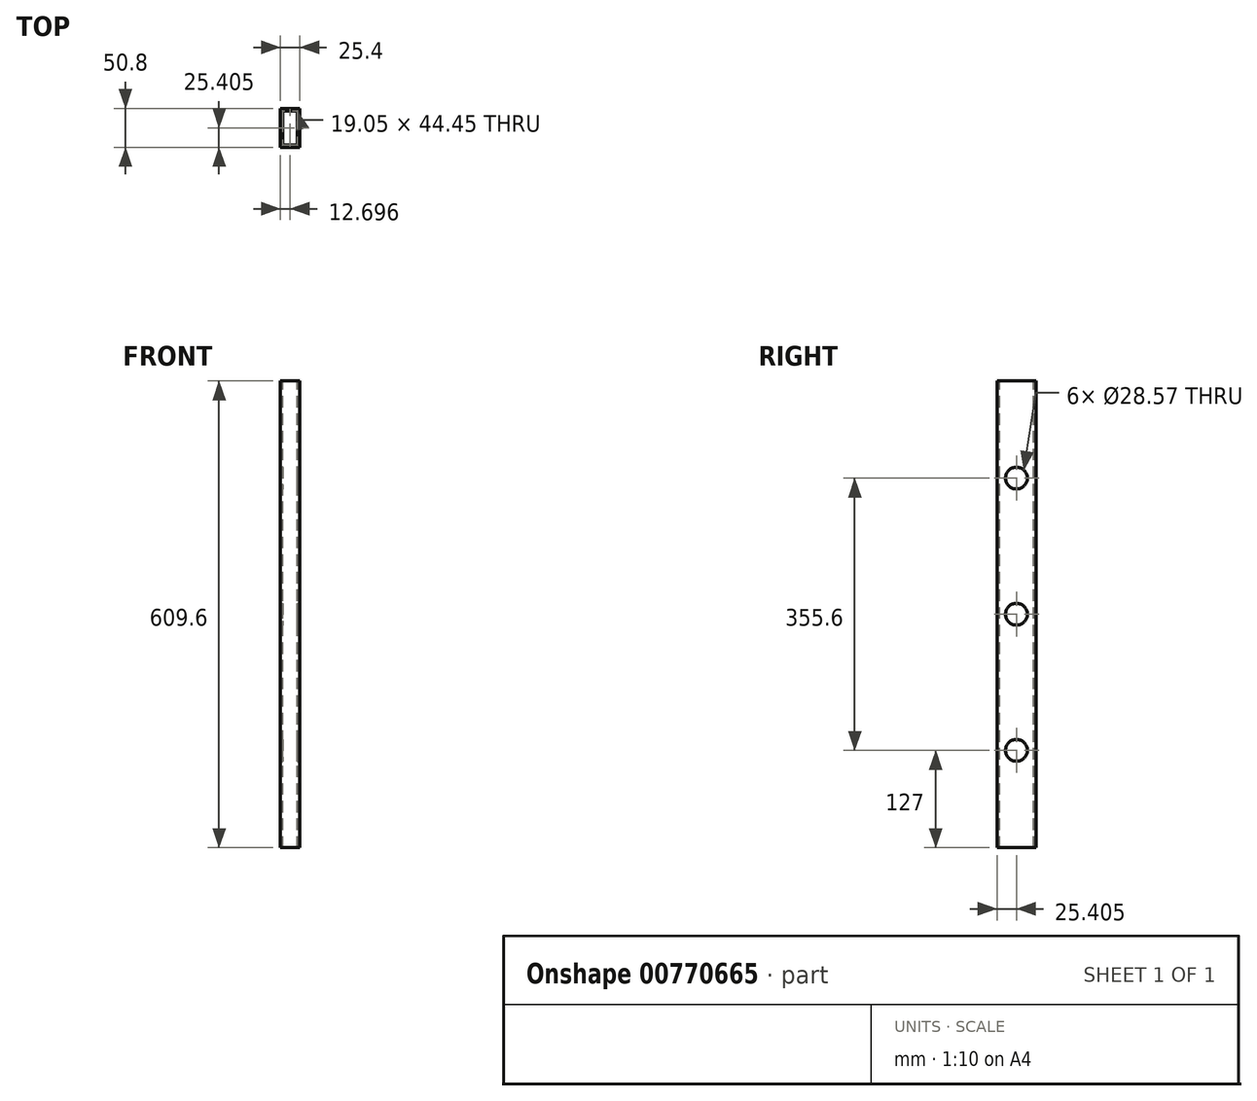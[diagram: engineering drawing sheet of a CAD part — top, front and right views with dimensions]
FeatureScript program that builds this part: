
annotation { "Feature Type Name" : "Feature", "Feature Type Description" : "" }
export const myFeature = defineFeature(function(context is Context, id is Id, definition is map)
    precondition{}
    {
        {
            var Q0;
            Q0=qCreatedBy(makeId("Top.planeOp"),FACE);
            var sketch = newSketch(context, id + "F0", { "sketchPlane" : qUnion([Q0])});
            skLineSegment(sketch, "E0.bottom", {"start": v(-17.82, 49.84) * mm, "end": v(7.58, 49.84) * mm});
            skLineSegment(sketch, "E0.top", {"start": v(-17.82, -0.96) * mm, "end": v(7.58, -0.96) * mm});
            skLineSegment(sketch, "E0.left", {"start": v(-17.82, 49.84) * mm, "end": v(-17.82, -0.96) * mm});
            skLineSegment(sketch, "E0.right", {"start": v(7.58, 49.84) * mm, "end": v(7.58, -0.96) * mm});
            skSolve(sketch);
        }
        {
            var Q0;
            Q0 = qSketchRegion(id + "F0", true);
            extrude(context, id + "F1", {"entities" : qUnion([Q0]), "depth" : 609.6 * mm, "offsetDistance" : 25.4 * mm});
        }
        {
            var Q0;
            Q0=makeQuery(id+"F1.opExtrude","CAP_FACE",FACE,{"disambiguationData":[OSD([sQuery(id+"F0.wireOp",EDGE,"E0.bottom"),sQuery(id+"F0.wireOp",EDGE,"E0.top"),sQuery(id+"F0.wireOp",EDGE,"E0.left"),sQuery(id+"F0.wireOp",EDGE,"E0.right")])],"isStart":false});
            var sketch = newSketch(context, id + "F2", { "sketchPlane" : qUnion([Q0])});
            skLineSegment(sketch, "E1.bottom", {"start": v(-14.65, 46.67) * mm, "end": v(4.4, 46.67) * mm});
            skLineSegment(sketch, "E1.top", {"start": v(-14.65, 2.22) * mm, "end": v(4.4, 2.22) * mm});
            skLineSegment(sketch, "E1.left", {"start": v(-14.65, 46.67) * mm, "end": v(-14.65, 2.22) * mm});
            skLineSegment(sketch, "E1.right", {"start": v(4.4, 46.67) * mm, "end": v(4.4, 2.22) * mm});
            skSolve(sketch);
        }
        {
            var Q0;
            Q0=makeQuery(id+"F2.imprint","IMPRINT",FACE,{"disambiguationData":[TD([[makeQuery(id+"F2.imprint","IMPRINT",EDGE,{"derivedFrom":sQuery(id+"F2.wireOp",EDGE,"E1.bottom")}),-1.0]])]});
            extrude(context, id + "F3", {"entities" : qUnion([Q0]), "operationType" : NewBodyOperationType.REMOVE, "oppositeDirection" : true, "depth" : 670.56 * mm, "offsetDistance" : 25.4 * mm});
        }
        {
            var Q0;
            Q0=makeQuery(id+"F1.opExtrude","SWEPT_FACE",FACE,{"disambiguationData":[OSD([sQuery(id+"F0.wireOp",EDGE,"E0.right")])]});
            var sketch = newSketch(context, id + "F4", { "sketchPlane" : qUnion([Q0])});
            skCircle(sketch, "E2", {"center": v(24.44, 304.8) * mm, "radius": 14.29 * mm});
            skCircle(sketch, "E3", {"center": v(24.44, 482.6) * mm, "radius": 14.29 * mm});
            skPoint(sketch, "E4.centerSnap0", {"position": v(24.44, 0) * mm});
            skCircle(sketch, "E5", {"center": v(24.44, 127) * mm, "radius": 14.29 * mm});
            skSolve(sketch);
        }
        {
            var Q0;
            Q0=makeQuery(id+"F4.imprint","IMPRINT",FACE,{"disambiguationData":[TD([[makeQuery(id+"F4.imprint","IMPRINT",EDGE,{"derivedFrom":sQuery(id+"F4.wireOp",EDGE,"E2")}),1.0]])]});
            var Q1;
            Q1=makeQuery(id+"F4.imprint","IMPRINT",FACE,{"disambiguationData":[TD([[makeQuery(id+"F4.imprint","IMPRINT",EDGE,{"derivedFrom":sQuery(id+"F4.wireOp",EDGE,"E3")}),1.0]])]});
            var Q2;
            Q2=makeQuery(id+"F4.imprint","IMPRINT",FACE,{"disambiguationData":[TD([[makeQuery(id+"F4.imprint","IMPRINT",EDGE,{"derivedFrom":sQuery(id+"F4.wireOp",EDGE,"E5")}),1.0]])]});
            extrude(context, id + "F5", {"entities" : qUnion([Q0, Q1, Q2]), "operationType" : NewBodyOperationType.REMOVE, "oppositeDirection" : true, "depth" : 83.82 * mm, "offsetDistance" : 25.4 * mm});
        }
    });
